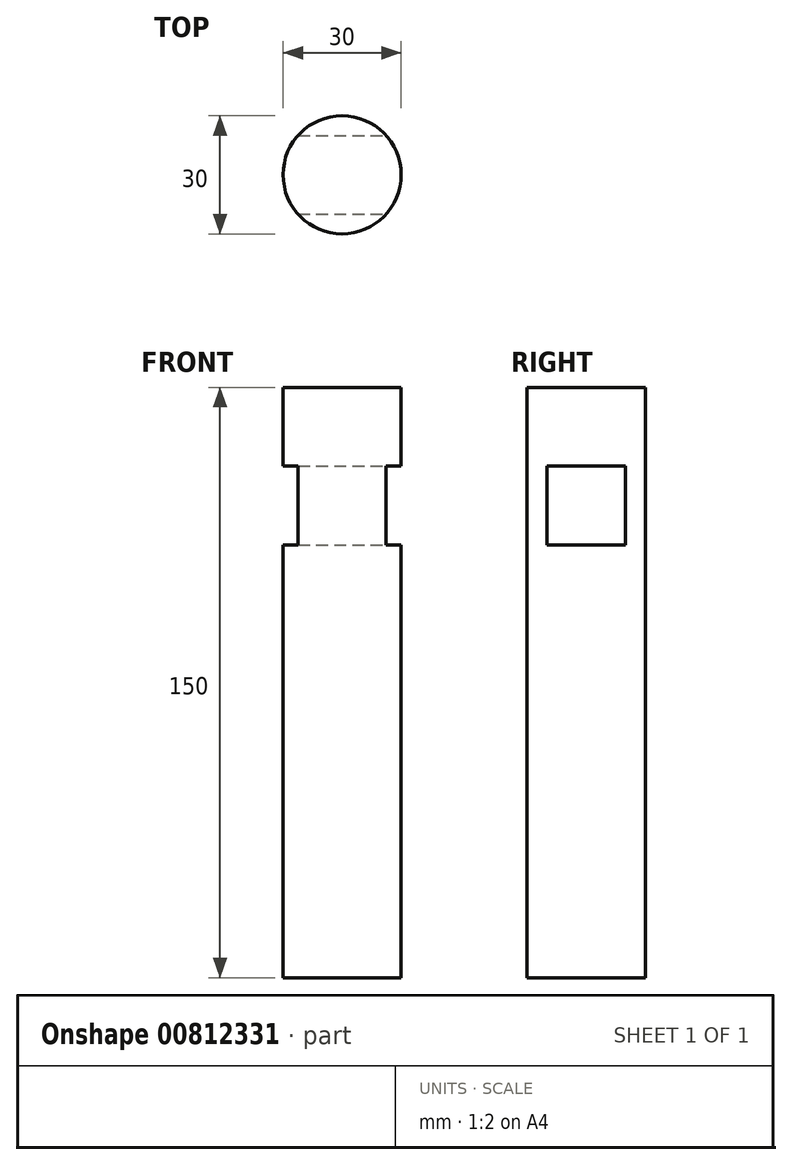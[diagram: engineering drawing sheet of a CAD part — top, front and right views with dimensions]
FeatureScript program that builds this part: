
annotation { "Feature Type Name" : "Feature", "Feature Type Description" : "" }
export const myFeature = defineFeature(function(context is Context, id is Id, definition is map)
    precondition{}
    {
        {
            var Q0;
            Q0=qCreatedBy(makeId("Top.planeOp"),FACE);
            var sketch = newSketch(context, id + "F0", { "sketchPlane" : qUnion([Q0])});
            skCircle(sketch, "E0", {"center": v(0, 0) * mm, "radius": 15 * mm});
            skSolve(sketch);
        }
        {
            var Q0;
            Q0=makeQuery(id+"F0.imprint","IMPRINT",FACE,{"disambiguationData":[TD([[makeQuery(id+"F0.imprint","IMPRINT",EDGE,{"derivedFrom":sQuery(id+"F0.wireOp",EDGE,"E0")}),1.0]])]});
            extrude(context, id + "F1", {"entities" : qUnion([Q0]), "depth" : 150 * mm, "offsetDistance" : 25 * mm});
        }
        {
            var Q0;
            Q0=qCreatedBy(makeId("Right.planeOp"),FACE);
            var sketch = newSketch(context, id + "F2", { "sketchPlane" : qUnion([Q0])});
            skLineSegment(sketch, "E1.bottom", {"start": v(10, 130) * mm, "end": v(-10, 130) * mm});
            skLineSegment(sketch, "E1.top", {"start": v(10, 110) * mm, "end": v(-10, 110) * mm});
            skLineSegment(sketch, "E1.left", {"start": v(10, 130) * mm, "end": v(10, 110) * mm});
            skLineSegment(sketch, "E1.right", {"start": v(-10, 130) * mm, "end": v(-10, 110) * mm});
            skSolve(sketch);
        }
        {
            var Q0;
            Q0 = qSketchRegion(id + "F2", true);
            extrude(context, id + "F3", {"entities" : qUnion([Q0]), "operationType" : NewBodyOperationType.REMOVE, "endBound" : BoundingType.SYMMETRIC, "oppositeDirection" : true, "depth" : 50 * mm, "offsetDistance" : 25 * mm});
        }
    });
